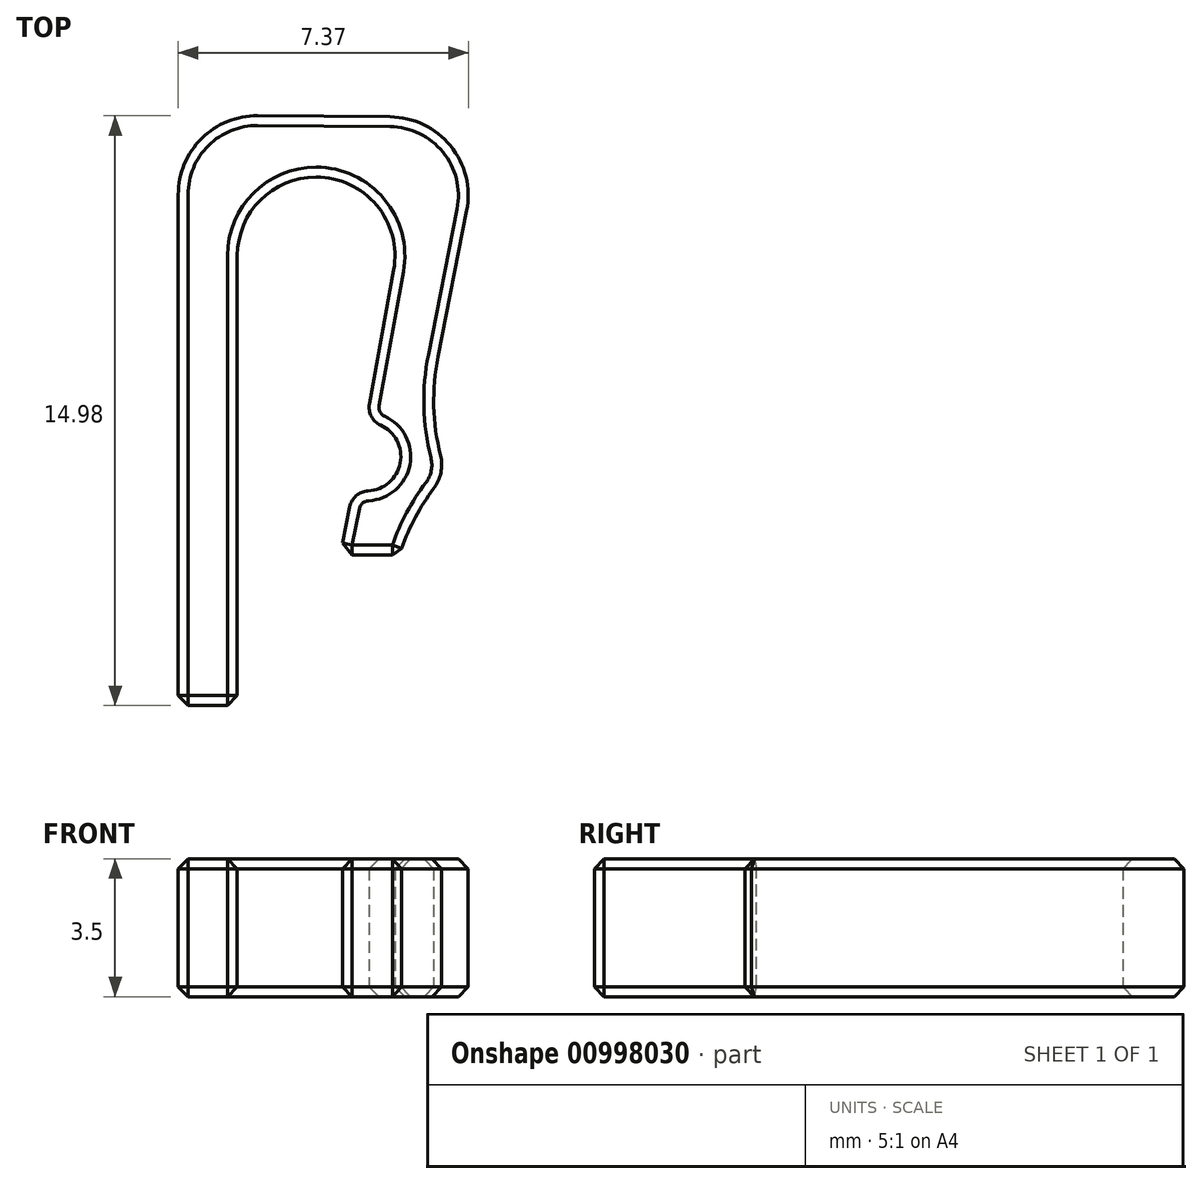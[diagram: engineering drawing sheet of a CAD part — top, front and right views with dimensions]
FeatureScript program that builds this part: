
annotation { "Feature Type Name" : "Feature", "Feature Type Description" : "" }
export const myFeature = defineFeature(function(context is Context, id is Id, definition is map)
    precondition{}
    {
        {
            var Q0;
            Q0=qCreatedBy(makeId("Top.planeOp"),FACE);
            var sketch = newSketch(context, id + "F0", { "sketchPlane" : qUnion([Q0])});
            skLineSegment(sketch, "E0.bottom", {"start": v(0, 0) * mm, "end": v(1.5, 0) * mm});
            skLineSegment(sketch, "E0.left", {"start": v(0, 0) * mm, "end": v(0, 15) * mm});
            skLineSegment(sketch, "E0.right", {"start": v(1.5, 0) * mm, "end": v(1.5, 13.42) * mm});
            skLineSegment(sketch, "E1", {"start": v(3.36, 0) * mm, "end": v(4.86, 0) * mm});
            skArc(sketch, "E2", {"start": v(5.88, 5.13) * mm, "mid": v(6.67, 5.92) * mm, "end": v(6.22, 6.96) * mm});
            skLineSegment(sketch, "E3", {"start": v(0, 15) * mm, "end": v(7.8, 14.93) * mm});
            skLineSegment(sketch, "E4", {"start": v(1.5, 13.42) * mm, "end": v(5.9, 13.42) * mm});
            skArc(sketch, "E5", {"start": v(4.45, 5.51) * mm, "mid": v(5.64, 6.16) * mm, "end": v(4.77, 7.2) * mm});
            skLineSegment(sketch, "E6.trimOffspring", {"start": v(4.45, 5.51) * mm, "end": v(3.36, 0) * mm});
            skLineSegment(sketch, "E7", {"start": v(4.77, 7.2) * mm, "end": v(5.9, 13.42) * mm});
            skLineSegment(sketch, "E8", {"start": v(6.22, 6.96) * mm, "end": v(7.8, 14.93) * mm});
            skLineSegment(sketch, "E9", {"start": v(4.86, 0) * mm, "end": v(5.88, 5.13) * mm});
            skLineSegment(sketch, "E10.bottom", {"start": v(6.43, -1.3) * mm, "end": v(3.08, -1.3) * mm});
            skLineSegment(sketch, "E10.top", {"start": v(6.43, 3.82) * mm, "end": v(3.08, 3.82) * mm});
            skLineSegment(sketch, "E10.left", {"start": v(6.43, -1.3) * mm, "end": v(6.43, 3.82) * mm});
            skLineSegment(sketch, "E10.right", {"start": v(3.08, -1.3) * mm, "end": v(3.08, 3.82) * mm});
            skSolve(sketch);
        }
        {
            var Q0;
            Q0=makeQuery(id+"F0.imprint","IMPRINT",FACE,{"disambiguationData":[TD([[makeQuery(id+"F0.imprint","IMPRINT",EDGE,{"derivedFrom":sQuery(id+"F0.wireOp",EDGE,"E0.bottom")}),1.0]])]});
            extrude(context, id + "F1", {"entities" : qUnion([Q0]), "depth" : 3.5 * mm, "offsetDistance" : 25 * mm});
        }
        {
            var Q0;
            Q0=makeQuery(id+"F1.opExtrude","SWEPT_EDGE",EDGE,{"disambiguationData":[OSD([sQuery(id+"F0.wireOp",EDGE,"IHRLUmcH-6XSx-FkSf-TKMu-dlJbMLICmPAX.left"),sQuery(id+"F0.wireOp",EDGE,"3e916993-07f4-4b3c-9848-dd47df8be342.trimOffspring")])]});
            var Q1;
            Q1=makeQuery(id+"F1.opExtrude","SWEPT_EDGE",EDGE,{"disambiguationData":[OSD([sQuery(id+"F0.wireOp",EDGE,"E2"),sQuery(id+"F0.wireOp",EDGE,"3e916993-07f4-4b3c-9848-dd47df8be342.trimOffspring")])]});
            var Q2;
            Q2=makeQuery(id+"F1.opExtrude","SWEPT_EDGE",EDGE,{"disambiguationData":[OSD([sQuery(id+"F0.wireOp",EDGE,"Ew0CDp9T-mxhx-iIfD-mCIr-3kt2pfTlOuVe"),sQuery(id+"F0.wireOp",EDGE,"E2")])]});
            var Q3;
            Q3=makeQuery(id+"F1.opExtrude","SWEPT_EDGE",EDGE,{"disambiguationData":[OSD([sQuery(id+"F0.wireOp",EDGE,"IHRLUmcH-6XSx-FkSf-TKMu-dlJbMLICmPAX.right"),sQuery(id+"F0.wireOp",EDGE,"efd65b54-6ed3-4fb0-9e64-8346d39dacc1.trimOffspring")])]});
            fillet(context, id + "F2", {"entities" : qUnion([Q0, Q1, Q2, Q3]), "radius" : 5.75 * mm, "tangentPropagation" : true, "allowEdgeOverflow" : false});
        }
        {
            var Q0;
            Q0=makeQuery(id+"F1.opExtrude","SWEPT_EDGE",EDGE,{"disambiguationData":[OSD([sQuery(id+"F0.wireOp",EDGE,"TkjvoKiQ-0piD-s0AE-E11K-Xd1oYQqU0Uqx"),sQuery(id+"F0.wireOp",EDGE,"efd65b54-6ed3-4fb0-9e64-8346d39dacc1.trimOffspring")])]});
            var Q1;
            Q1=makeQuery(id+"F1.opExtrude","SWEPT_EDGE",EDGE,{"disambiguationData":[OSD([sQuery(id+"F0.wireOp",EDGE,"TkjvoKiQ-0piD-s0AE-E11K-Xd1oYQqU0Uqx"),sQuery(id+"F0.wireOp",EDGE,"dC64C05I-tYbY-RY9d-S9Bg-WALaEgUDzWnN")])]});
            var Q2;
            Q2=makeQuery(id+"F1.opExtrude","SWEPT_EDGE",EDGE,{"disambiguationData":[OSD([sQuery(id+"F0.wireOp",EDGE,"E5"),sQuery(id+"F0.wireOp",EDGE,"E6.trimOffspring")])]});
            var Q3;
            Q3=makeQuery(id+"F1.opExtrude","SWEPT_EDGE",EDGE,{"disambiguationData":[OSD([sQuery(id+"F0.wireOp",EDGE,"E5"),sQuery(id+"F0.wireOp",EDGE,"E7")])]});
            fillet(context, id + "F3", {"entities" : qUnion([Q0, Q1, Q2, Q3]), "radius" : .5 * mm, "tangentPropagation" : true, "allowEdgeOverflow" : false});
        }
        {
            var Q0;
            Q0=makeQuery(id+"F1.opExtrude","SWEPT_EDGE",EDGE,{"disambiguationData":[OSD([sQuery(id+"F0.wireOp",EDGE,"IHRLUmcH-6XSx-FkSf-TKMu-dlJbMLICmPAX.left"),sQuery(id+"F0.wireOp",EDGE,"E3")])]});
            var Q1;
            Q1=makeQuery(id+"F2.opFillet","BLEND_EDGE",EDGE,{"blendedFrom":[makeQuery(id+"F1.opExtrude","SWEPT_EDGE",EDGE,{"disambiguationData":[OSD([sQuery(id+"F0.wireOp",EDGE,"IHRLUmcH-6XSx-FkSf-TKMu-dlJbMLICmPAX.right"),sQuery(id+"F0.wireOp",EDGE,"E4")])]}),makeQuery(id+"F1.opExtrude","SWEPT_FACE",FACE,{"disambiguationData":[OSD([sQuery(id+"F0.wireOp",EDGE,"E0.right")])]})],"blendedInto":[makeQuery(id+"F1.opExtrude","SWEPT_FACE",FACE,{"disambiguationData":[OSD([sQuery(id+"F0.wireOp",EDGE,"E0.right")])]})]});
            var Q2;
            Q2=makeQuery(id+"F1.opExtrude","SWEPT_EDGE",EDGE,{"disambiguationData":[OSD([sQuery(id+"F0.wireOp",EDGE,"E0.left"),sQuery(id+"F0.wireOp",EDGE,"E3")])]});
            var Q3;
            Q3=makeQuery(id+"F1.opExtrude","SWEPT_EDGE",EDGE,{"disambiguationData":[OSD([sQuery(id+"F0.wireOp",EDGE,"IHRLUmcH-6XSx-FkSf-TKMu-dlJbMLICmPAX.right"),sQuery(id+"F0.wireOp",EDGE,"E4")])]});
            var Q4;
            Q4=makeQuery(id+"F1.opExtrude","SWEPT_EDGE",EDGE,{"disambiguationData":[OSD([sQuery(id+"F0.wireOp",EDGE,"E0.right"),sQuery(id+"F0.wireOp",EDGE,"E4")])]});
            fillet(context, id + "F4", {"entities" : qUnion([Q0, Q1, Q2, Q3, Q4]), "radius" : 2 * mm, "tangentPropagation" : true, "allowEdgeOverflow" : false});
        }
        {
            var Q0;
            Q0=makeQuery(id+"F1.opExtrude","CAP_FACE",FACE,{"disambiguationData":[OSD([sQuery(id+"F0.wireOp",EDGE,"E0.bottom"),sQuery(id+"F0.wireOp",EDGE,"E0.left"),sQuery(id+"F0.wireOp",EDGE,"E0.right"),sQuery(id+"F0.wireOp",EDGE,"EUyIurIN-PLQ4-0Xmk-S0Dv-sKdYLnjtQCLd.top"),sQuery(id+"F0.wireOp",EDGE,"IHRLUmcH-6XSx-FkSf-TKMu-dlJbMLICmPAX.left"),sQuery(id+"F0.wireOp",EDGE,"IHRLUmcH-6XSx-FkSf-TKMu-dlJbMLICmPAX.right"),sQuery(id+"F0.wireOp",EDGE,"TkjvoKiQ-0piD-s0AE-E11K-Xd1oYQqU0Uqx"),sQuery(id+"F0.wireOp",EDGE,"dC64C05I-tYbY-RY9d-S9Bg-WALaEgUDzWnN"),sQuery(id+"F0.wireOp",EDGE,"E1"),sQuery(id+"F0.wireOp",EDGE,"Ew0CDp9T-mxhx-iIfD-mCIr-3kt2pfTlOuVe"),sQuery(id+"F0.wireOp",EDGE,"E2"),sQuery(id+"F0.wireOp",EDGE,"efd65b54-6ed3-4fb0-9e64-8346d39dacc1.trimOffspring"),sQuery(id+"F0.wireOp",EDGE,"3e916993-07f4-4b3c-9848-dd47df8be342.trimOffspring"),sQuery(id+"F0.wireOp",EDGE,"pv0PMX2H-hX43-qpVY-PXb7-XsbNURAUq7CL")])],"isStart":true});
            var Q1;
            Q1=makeQuery(id+"F1.opExtrude","CAP_FACE",FACE,{"disambiguationData":[OSD([sQuery(id+"F0.wireOp",EDGE,"E0.bottom"),sQuery(id+"F0.wireOp",EDGE,"E0.left"),sQuery(id+"F0.wireOp",EDGE,"E0.right"),sQuery(id+"F0.wireOp",EDGE,"EUyIurIN-PLQ4-0Xmk-S0Dv-sKdYLnjtQCLd.top"),sQuery(id+"F0.wireOp",EDGE,"IHRLUmcH-6XSx-FkSf-TKMu-dlJbMLICmPAX.left"),sQuery(id+"F0.wireOp",EDGE,"IHRLUmcH-6XSx-FkSf-TKMu-dlJbMLICmPAX.right"),sQuery(id+"F0.wireOp",EDGE,"TkjvoKiQ-0piD-s0AE-E11K-Xd1oYQqU0Uqx"),sQuery(id+"F0.wireOp",EDGE,"dC64C05I-tYbY-RY9d-S9Bg-WALaEgUDzWnN"),sQuery(id+"F0.wireOp",EDGE,"E1"),sQuery(id+"F0.wireOp",EDGE,"Ew0CDp9T-mxhx-iIfD-mCIr-3kt2pfTlOuVe"),sQuery(id+"F0.wireOp",EDGE,"E2"),sQuery(id+"F0.wireOp",EDGE,"efd65b54-6ed3-4fb0-9e64-8346d39dacc1.trimOffspring"),sQuery(id+"F0.wireOp",EDGE,"3e916993-07f4-4b3c-9848-dd47df8be342.trimOffspring"),sQuery(id+"F0.wireOp",EDGE,"pv0PMX2H-hX43-qpVY-PXb7-XsbNURAUq7CL")])],"isStart":false});
            var Q2;
            Q2=makeQuery(id+"F1.opExtrude","SWEPT_FACE",FACE,{"disambiguationData":[OSD([sQuery(id+"F0.wireOp",EDGE,"E1")])]});
            var Q3;
            Q3=makeQuery(id+"F1.opExtrude","SWEPT_FACE",FACE,{"disambiguationData":[OSD([sQuery(id+"F0.wireOp",EDGE,"E0.bottom")])]});
            var Q4;
            Q4=makeQuery(id+"F1.opExtrude","SWEPT_EDGE",EDGE,{"disambiguationData":[OSD([sQuery(id+"F0.wireOp",EDGE,"E6.trimOffspring"),sQuery(id+"F0.wireOp",EDGE,"E10.top")])]});
            var Q5;
            Q5=makeQuery(id+"F2.opFillet","BLEND_EDGE",EDGE,{"blendedFrom":[makeQuery(id+"F1.opExtrude","SWEPT_EDGE",EDGE,{"disambiguationData":[OSD([sQuery(id+"F0.wireOp",EDGE,"E2"),sQuery(id+"F0.wireOp",EDGE,"E9")])]}),makeQuery(id+"F1.opExtrude","SWEPT_FACE",FACE,{"disambiguationData":[OSD([sQuery(id+"F0.wireOp",EDGE,"E10.top")])]})],"blendedInto":[makeQuery(id+"F1.opExtrude","SWEPT_FACE",FACE,{"disambiguationData":[OSD([sQuery(id+"F0.wireOp",EDGE,"E10.top")])]})]});
            chamfer(context, id + "F5", {"entities" : qUnion([Q0, Q1, Q2, Q3, Q4, Q5]), "width" : .25 * mm, "tangentPropagation" : true});
        }
    });
